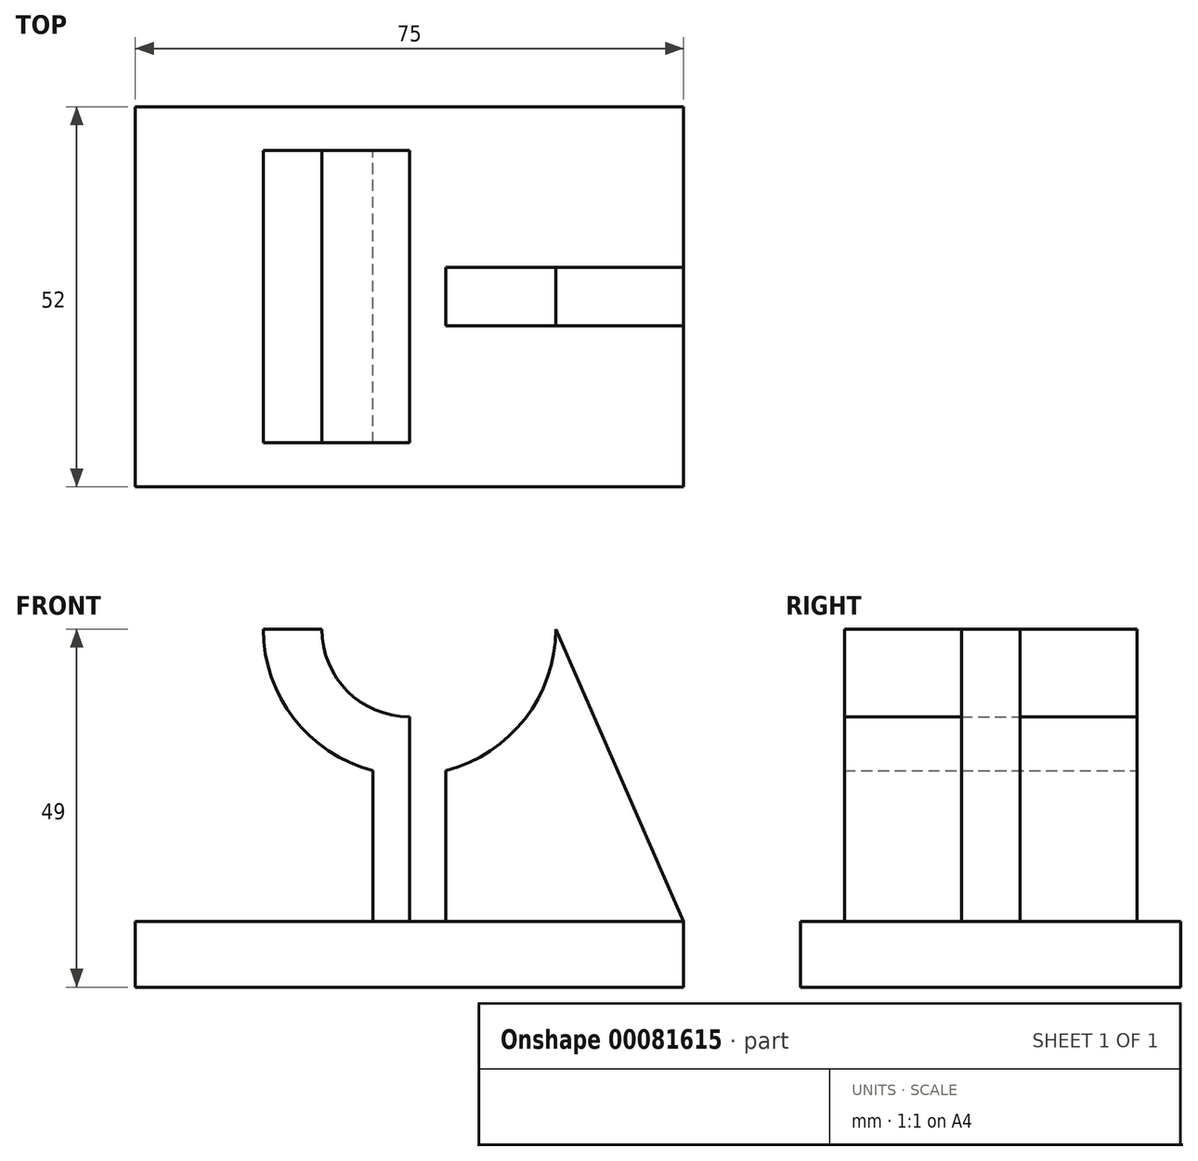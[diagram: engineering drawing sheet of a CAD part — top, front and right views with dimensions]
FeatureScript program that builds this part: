
annotation { "Feature Type Name" : "Feature", "Feature Type Description" : "" }
export const myFeature = defineFeature(function(context is Context, id is Id, definition is map)
    precondition{}
    {
        {
            var Q0;
            Q0=qCreatedBy(makeId("Front.planeOp"),FACE);
            var sketch = newSketch(context, id + "F0", { "sketchPlane" : qUnion([Q0])});
            skLineSegment(sketch, "E0", {"start": v(0, 0) * mm, "end": v(0, 98) * mm, "construction": true});
            skLineSegment(sketch, "E1.bottom", {"start": v(0, 0) * mm, "end": v(37.5, 0) * mm});
            skLineSegment(sketch, "E1.top", {"start": v(0, 9) * mm, "end": v(37.5, 9) * mm});
            skLineSegment(sketch, "E1.left", {"start": v(0, 0) * mm, "end": v(0, 9) * mm});
            skLineSegment(sketch, "E1.right", {"start": v(37.5, 0) * mm, "end": v(37.5, 9) * mm});
            skLineSegment(sketch, "E2.bottom", {"start": v(0, 9) * mm, "end": v(5, 9) * mm});
            skLineSegment(sketch, "E2.left", {"start": v(0, 9) * mm, "end": v(0, 33.61) * mm});
            skLineSegment(sketch, "E2.right", {"start": v(5, 9) * mm, "end": v(5, 29.64) * mm});
            skArc(sketch, "E3", {"start": v(5, 29.64) * mm, "mid": v(15.81, 36.75) * mm, "end": v(20, 49) * mm});
            skArc(sketch, "E4", {"start": v(0, 37) * mm, "mid": v(8.49, 40.51) * mm, "end": v(12, 49) * mm});
            skLineSegment(sketch, "E5", {"start": v(12, 49) * mm, "end": v(20, 49) * mm});
            skLineSegment(sketch, "E6", {"start": v(0, 37) * mm, "end": v(0, 33.61) * mm});
            skLineSegment(sketch, "E7", {"start": v(20, 49) * mm, "end": v(37.5, 9) * mm});
            skArc(sketch, "E8.MirrorCS", {"start": v(0, 37) * mm, "mid": v(-8.49, 40.51) * mm, "end": v(-12, 49) * mm});
            skArc(sketch, "E9.MirrorCS", {"start": v(-5, 29.64) * mm, "mid": v(-15.81, 36.75) * mm, "end": v(-20, 49) * mm});
            skLineSegment(sketch, "E10.MirrorCS", {"start": v(-20, 49) * mm, "end": v(-37.5, 9) * mm});
            skLineSegment(sketch, "E11.MirrorCS", {"start": v(-12, 49) * mm, "end": v(-20, 49) * mm});
            skLineSegment(sketch, "E12.MirrorCS", {"start": v(-37.5, 0) * mm, "end": v(-37.5, 9) * mm});
            skLineSegment(sketch, "E13.MirrorCS", {"start": v(0, 0) * mm, "end": v(-37.5, 0) * mm});
            skLineSegment(sketch, "E14.MirrorCS", {"start": v(-5, 9) * mm, "end": v(-5, 29.64) * mm});
            skLineSegment(sketch, "E15.MirrorCS", {"start": v(0, 9) * mm, "end": v(-37.5, 9) * mm});
            skPoint(sketch, "E16.MirrorCS.end.orphan", {"position": v(-5, 29.64) * mm});
            skPoint(sketch, "E16.MirrorCS.start.orphan", {"position": v(0, 33.61) * mm});
            skSolve(sketch);
        }
        {
            var Q0;
            {var subQ1=sQuery(id+"F0.wireOp",EDGE,"E1.left");Q0=makeQuery(id+"F0.imprint","IMPRINT",FACE,{"disambiguationData":[TD([[makeQuery(id+"F0.imprint","IMPRINT",EDGE,{"derivedFrom":subQ1}),1.0]])]});}
            var Q1;
            Q1=makeQuery(id+"F0.imprint","IMPRINT",FACE,{"disambiguationData":[TD([[makeQuery(id+"F0.imprint","IMPRINT",EDGE,{"derivedFrom":sQuery(id+"F0.wireOp",EDGE,"E1.bottom")}),1.0]])]});
            extrude(context, id + "F1", {"entities" : qUnion([Q0, Q1]), "endBound" : BoundingType.SYMMETRIC, "depth" : 52 * mm});
        }
        {
            var Q0;
            {var subQ0=sQuery(id+"F0.wireOp",EDGE,"E2.left");Q0=makeQuery(id+"F0.imprint","IMPRINT",FACE,{"disambiguationData":[TD([[makeQuery(id+"F0.imprint","IMPRINT",EDGE,{"derivedFrom":subQ0}),1.0]])]});}
            var Q1;
            Q1=makeQuery(id+"F0.imprint","IMPRINT",FACE,{"disambiguationData":[TD([[makeQuery(id+"F0.imprint","IMPRINT",EDGE,{"derivedFrom":sQuery(id+"F0.wireOp",EDGE,"E2.bottom")}),1.0]])]});
            extrude(context, id + "F2", {"entities" : qUnion([Q0, Q1]), "operationType" : NewBodyOperationType.ADD, "endBound" : BoundingType.SYMMETRIC, "depth" : 40 * mm});
        }
        {
            var Q0;
            Q0=makeQuery(id+"F0.imprint","IMPRINT",FACE,{"disambiguationData":[TD([[makeQuery(id+"F0.imprint","IMPRINT",EDGE,{"derivedFrom":sQuery(id+"F0.wireOp",EDGE,"E9.MirrorCS")}),1.0]])]});
            var Q1;
            Q1=makeQuery(id+"F0.imprint","IMPRINT",FACE,{"disambiguationData":[TD([[makeQuery(id+"F0.imprint","IMPRINT",EDGE,{"derivedFrom":sQuery(id+"F0.wireOp",EDGE,"E1.top")}),1.0]])]});
            extrude(context, id + "F3", {"entities" : qUnion([Q0, Q1]), "operationType" : NewBodyOperationType.ADD, "endBound" : BoundingType.SYMMETRIC, "depth" : 8 * mm});
        }
    });
